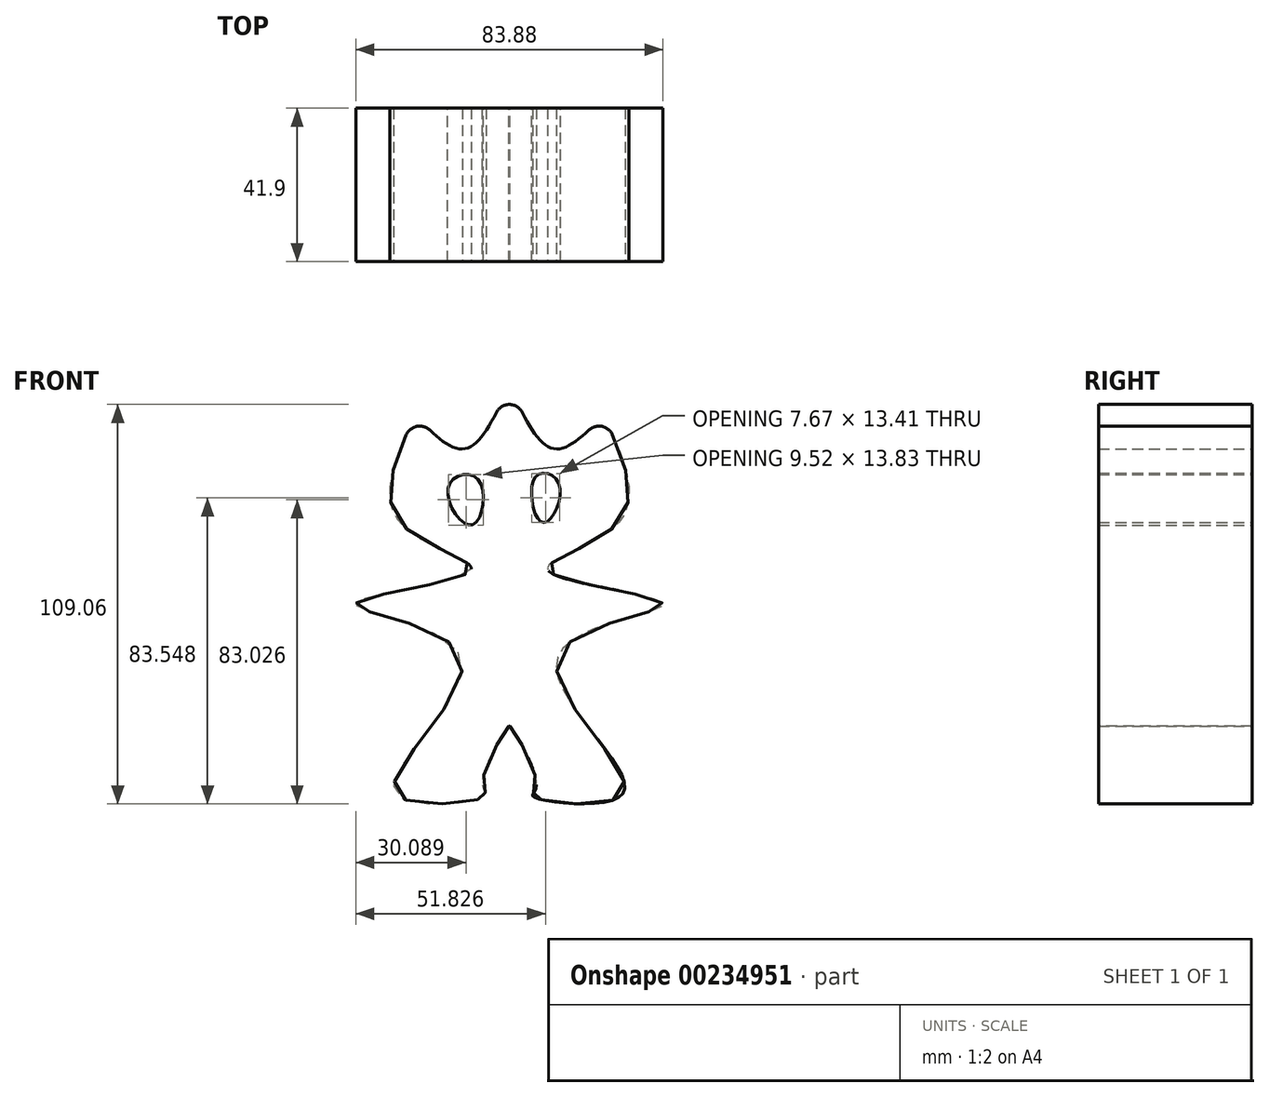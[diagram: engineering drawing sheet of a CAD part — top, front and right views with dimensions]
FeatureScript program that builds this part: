
annotation { "Feature Type Name" : "Feature", "Feature Type Description" : "" }
export const myFeature = defineFeature(function(context is Context, id is Id, definition is map)
    precondition{}
    {
        {
            var Q0;
            Q0=qCreatedBy(makeId("Front.planeOp"),FACE);
            var sketch = newSketch(context, id + "F0", { "sketchPlane" : qUnion([Q0])});
            skFitSpline(sketch, "E0", {"points": [v(0, 50.96) * mm, v(12.04, 33.35) * mm, v(25.7, 42.39) * mm], "startDerivative": vector(20.82, -46.98) * mm, "endDerivative": vector(30.81, 31.57) * mm});
            skFitSpline(sketch, "E1", {"points": [v(25.7, 42.39) * mm, v(29.42, 12.74) * mm, v(10.65, 0) * mm, v(41.92, -9.03) * mm, v(13.2, -23.63) * mm, v(31.27, -60.45) * mm, v(6.49, -61.61) * mm, v(7.41, -58.83) * mm, v(0, -42.39) * mm, v(0, -43.31) * mm], "startDerivative": vector(115.36, -244.73) * mm, "endDerivative": vector(12.95, -62.81) * mm});
            skFitSpline(sketch, "E2.MirrorCS", {"points": [v(0, 50.96) * mm, v(-12.04, 33.35) * mm, v(-25.7, 42.39) * mm], "startDerivative": vector(-20.82, -46.98) * mm, "endDerivative": vector(-30.81, 31.57) * mm});
            skFitSpline(sketch, "E3.MirrorCS", {"points": [v(-25.7, 42.39) * mm, v(-29.42, 12.74) * mm, v(-10.65, 0) * mm, v(-41.92, -9.03) * mm, v(-13.2, -23.63) * mm, v(-31.27, -60.45) * mm, v(-6.49, -61.61) * mm, v(-7.41, -58.83) * mm, v(0, -42.39) * mm, v(0, -43.31) * mm], "startDerivative": vector(-115.36, -244.73) * mm, "endDerivative": vector(-12.95, -62.81) * mm});
            skFitSpline(sketch, "E4", {"points": [v(7.18, 25.7) * mm, v(9.03, 13.2) * mm, v(13.67, 23.4) * mm, v(7.18, 25.7) * mm]});
            skFitSpline(sketch, "E5", {"points": [v(-8.57, 25.01) * mm, v(-10.2, 12.5) * mm, v(-16.68, 22.93) * mm, v(-8.57, 25.01) * mm]});
            skSolve(sketch);
        }
        {
            var Q0;
            {var subQ5=sQuery(id+"F0.wireOp",EDGE,"E0");Q0=makeQuery(id+"F0.imprint","IMPRINT",FACE,{"disambiguationData":[TD([[makeQuery(id+"F0.imprint","IMPRINT",EDGE,{"derivedFrom":subQ5}),-1.0]])]});}
            extrude(context, id + "F1", {"entities" : qUnion([Q0]), "depth" : 41.9 * mm});
        }
        {
            var Q0;
            Q0=makeQuery(id+"F1.opExtrude","SWEPT_EDGE",EDGE,{"disambiguationData":[OSD([sQuery(id+"F0.wireOp",EDGE,"E2.MirrorCS"),sQuery(id+"F0.wireOp",EDGE,"E3.MirrorCS")])]});
            var Q1;
            Q1=makeQuery(id+"F1.opExtrude","SWEPT_EDGE",EDGE,{"disambiguationData":[OSD([sQuery(id+"F0.wireOp",EDGE,"E0"),sQuery(id+"F0.wireOp",EDGE,"E2.MirrorCS")])]});
            var Q2;
            Q2=makeQuery(id+"F1.opExtrude","SWEPT_EDGE",EDGE,{"disambiguationData":[OSD([sQuery(id+"F0.wireOp",EDGE,"E0"),sQuery(id+"F0.wireOp",EDGE,"E1")])]});
            fillet(context, id + "F2", {"entities" : qUnion([Q0, Q1, Q2]), "radius" : 4 * mm, "tangentPropagation" : true, "allowEdgeOverflow" : false});
        }
    });
